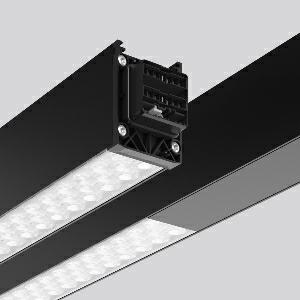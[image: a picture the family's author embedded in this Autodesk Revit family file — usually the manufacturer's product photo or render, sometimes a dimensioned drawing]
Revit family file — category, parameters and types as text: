
# Revit family: linedo_2_3m_90_1000_952390_853_776_702_4c96
name_source: partatom
category: Lighting Fixtures
units: mm (PartAtom-declared; Revit-internal decimal feet)

## family parameters
Cut with Voids When Loaded = No
Host = Face
Light Source = No
Part Type = Normal
Room Calculation Point = No
Round Connector Dimension = Use Diameter
Shared = No

## types (1)
- LINEDO_2,3m_90_1000 (1 x LED Modul 850, 3400 lm, 5000)
    Apparent Load = 23 VA
    CIE Flux Codes = 73 96 99 100 100
    Color Rendering = 80
    Color Temperature = 5000
    Default Elevation = 1800 mm
    Description = LINEDO, 23 W, 3400 lm, 850, black, DALI
Continuous line luminaire, L 2291 B 58 H 76
    Height = 76 mm
    Lamp = 1 x LED Modul 850
    Lamp Light Flux = 3400 lm
    Lamp count = 1
    Length = 2291 mm
    Lifetime = 50000 h
    Luminous efficacy = 148 lm/W
    Manufacturer = RZB
    ModVariant = No
    Model = 952390.853.776.702
    Mounting Place = Ceiling
    Mounting Type = Surface mounted, Pendant
    Number of Poles = 1
    OnlyDefault = Yes
    Power Factor = 1
    Product Name = LINEDO_2,3m_90_1000
    Product group = Surface mounted continuous line luminaire system
    ProductGroupID = 310
    Protection Class = Protection class I
    Protection Degree = IP 54
    RLX_Detail_Level = 1
    RLX_Emergency_Light_Flux = 0 lm
    RLX_Emergency_Type = 0
    RLX_Emergency_Type_DB = No
    RlxData = <blob elided: 56545 chars, md5=d4df467c>
    Socket = socket
    Standby Power = 0 W
    System Light Flux = 3400 lm
    System Power = 23 W
    Type Comments = Product without accessories
    Type Image = 954590.853.476.504.jpg
    URL = http://relux.com
    VarID = ---
    Voltage = 230 V
    Voltage Range = 220-240 V
    Weight = 0.00 kg
    Width = 58 mm

## geometry (parser evidence)
native form markers: Blend x4, Sweep x14
no freeform markers — native parametric forms only
